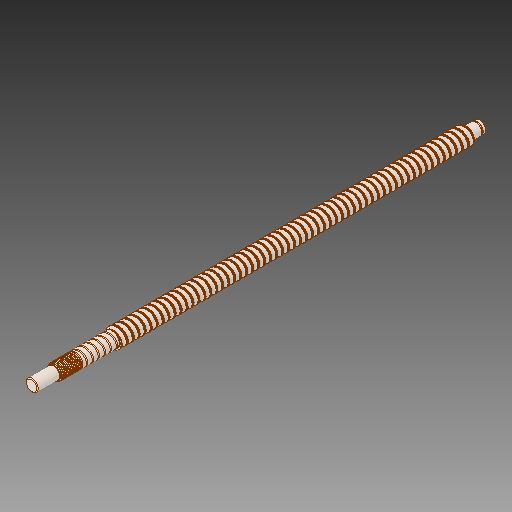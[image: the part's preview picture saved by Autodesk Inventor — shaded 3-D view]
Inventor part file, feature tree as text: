
AUTODESK INVENTOR PART (.ipt)
format: ipt  version: 2018 (Build 220112000, 112)  size: 3,510,272 bytes
history: native  units: mm
features: other x3, thread x1
ambient origin geometry x8: Origin, YZ Plane, XZ Plane, XY Plane, X Axis, Y Axis, Z Axis, Center Point
bodies: Body1 (feature_tree), Body2 (feature_tree)
feature tree (4):
  other  "Sólido1"
  other  "Sólido2"
  thread  "Thread M10x1.0 End[1]"  [1 undecoded]
  other  "Aesthetic Chamfer"
note: 1 required parameter value undecoded (feature->parameter linkage not recoverable at this tier; creation-order binding heuristic only, values carry confidence <= 0.55)
